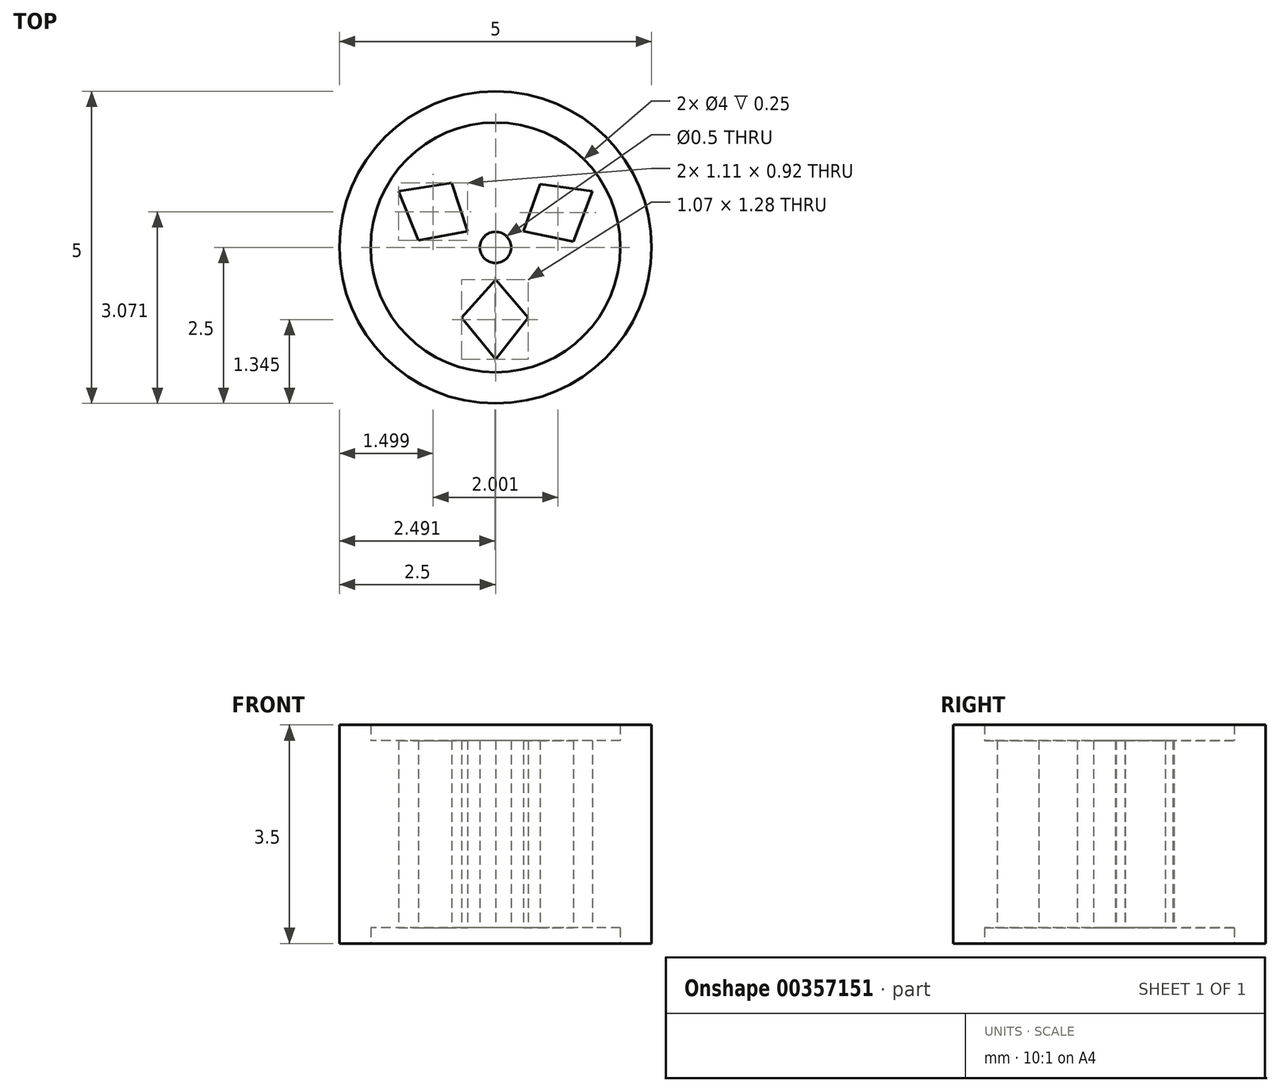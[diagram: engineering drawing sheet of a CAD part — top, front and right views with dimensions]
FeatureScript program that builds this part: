
annotation { "Feature Type Name" : "Feature", "Feature Type Description" : "" }
export const myFeature = defineFeature(function(context is Context, id is Id, definition is map)
    precondition{}
    {
        {
            var Q0;
            Q0=qCreatedBy(makeId("Top.planeOp"),FACE);
            var sketch = newSketch(context, id + "F0", { "sketchPlane" : qUnion([Q0])});
            skCircle(sketch, "E0", {"center": v(0, 0) * mm, "radius": 2 * mm});
            skCircle(sketch, "E1", {"center": v(0, 0) * mm, "radius": 2.5 * mm});
            skCircle(sketch, "E2", {"center": v(0, 0) * mm, "radius": 0.25 * mm});
            skLineSegment(sketch, "E3", {"start": v(0, -1.8) * mm, "end": v(0, -0.52) * mm});
            skLineSegment(sketch, "E4", {"start": v(0, -0.52) * mm, "end": v(-0.54, -1.13) * mm});
            skLineSegment(sketch, "E5", {"start": v(-0.54, -1.13) * mm, "end": v(0.52, -1.13) * mm});
            skLineSegment(sketch, "E6", {"start": v(0.52, -1.13) * mm, "end": v(0, -0.52) * mm});
            skLineSegment(sketch, "E7", {"start": v(0, -1.8) * mm, "end": v(-0.54, -1.13) * mm});
            skLineSegment(sketch, "E8", {"start": v(0, -1.8) * mm, "end": v(0.52, -1.13) * mm});
            skLineSegment(sketch, "E9.1.0", {"start": v(-1.24, 0.1) * mm, "end": v(-0.45, 0.26) * mm});
            skLineSegment(sketch, "E9.1.1", {"start": v(-1.55, 0.9) * mm, "end": v(-0.45, 0.26) * mm});
            skLineSegment(sketch, "E9.1.2", {"start": v(-0.45, 0.26) * mm, "end": v(-0.7, 1.03) * mm});
            skLineSegment(sketch, "E9.1.3", {"start": v(-1.55, 0.9) * mm, "end": v(-0.7, 1.03) * mm});
            skLineSegment(sketch, "E9.1.4", {"start": v(-1.55, 0.9) * mm, "end": v(-1.24, 0.1) * mm});
            skLineSegment(sketch, "E9.1.5", {"start": v(-0.7, 1.03) * mm, "end": v(-1.24, 0.1) * mm});
            skLineSegment(sketch, "E9.2.0", {"start": v(0.71, 1.02) * mm, "end": v(0.45, 0.26) * mm});
            skLineSegment(sketch, "E9.2.1", {"start": v(1.55, 0.9) * mm, "end": v(0.45, 0.26) * mm});
            skLineSegment(sketch, "E9.2.2", {"start": v(0.45, 0.26) * mm, "end": v(1.25, 0.1) * mm});
            skLineSegment(sketch, "E9.2.3", {"start": v(1.55, 0.9) * mm, "end": v(1.25, 0.1) * mm});
            skLineSegment(sketch, "E9.2.4", {"start": v(1.55, 0.9) * mm, "end": v(0.71, 1.02) * mm});
            skLineSegment(sketch, "E9.2.5", {"start": v(1.25, 0.1) * mm, "end": v(0.71, 1.02) * mm});
            skLineSegment(sketch, "E9.anchor1", {"start": v(0, 0) * mm, "end": v(0, -1.8) * mm, "construction": true});
            skLineSegment(sketch, "E9.anchor2", {"start": v(0, 0) * mm, "end": v(1.55, 0.9) * mm, "construction": true});
            skSolve(sketch);
        }
        {
            var Q0;
            Q0=makeQuery(id+"F0.imprint","IMPRINT",FACE,{"disambiguationData":[TD([[makeQuery(id+"F0.imprint","IMPRINT",EDGE,{"derivedFrom":sQuery(id+"F0.wireOp",EDGE,"E0")}),1.0]])]});
            extrude(context, id + "F1", {"entities" : qUnion([Q0]), "endBound" : BoundingType.SYMMETRIC, "depth" : 3 * mm});
        }
        {
            var Q0;
            Q0=makeQuery(id+"F0.imprint","IMPRINT",FACE,{"disambiguationData":[TD([[makeQuery(id+"F0.imprint","IMPRINT",EDGE,{"derivedFrom":sQuery(id+"F0.wireOp",EDGE,"E0")}),-1.0]])]});
            extrude(context, id + "F2", {"entities" : qUnion([Q0]), "operationType" : NewBodyOperationType.ADD, "endBound" : BoundingType.SYMMETRIC, "depth" : 3.5 * mm});
        }
    });
